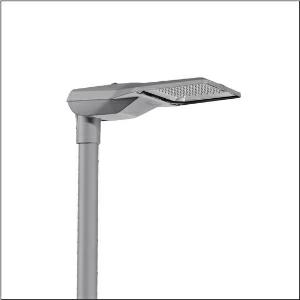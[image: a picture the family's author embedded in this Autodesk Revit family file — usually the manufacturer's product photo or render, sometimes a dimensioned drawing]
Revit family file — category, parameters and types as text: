
# Revit family: streetlight_sl_21_iq_midi___p0_8ab_5xe3r31v08mb_2caf
name_source: partatom
category: Lighting Fixtures
units: mm (PartAtom-declared; Revit-internal decimal feet)

## family parameters
Cut with Voids When Loaded = No
Host = Face
Light Source = No
Part Type = Normal
Room Calculation Point = No
Round Connector Dimension = Use Diameter
Shared = No

## types (1)
- --- (1 x LED, 15920 lm, 129.3 W, 3000K)
    Apparent Load = 129 VA
    CIE Flux Codes = 36 71 98 100 100
    Color Rendering = 70
    Color Temperature = 3000K
    Default Elevation = 1800 mm
    Description = Streetlight SL 21 iQ midi, mast luminaire, primary light control with lens, of PMMA, primary optical cover: cover, of toughened safety glass, transparent, light distribution: P0.8aB, light emission: direct distribution, primary light characteristic: asymmetric, installation type: post-top, side-entry, LED, High Power LED, rated luminous flux: 15.920lm, luminous efficacy: 123lm/W, light colour: 730, colour temperature: 3000K, control gear: iQ-Street Remote, D4i with power reduction, control: pre-setting: logarithmic dimming characteristic, Street-Remote, Auto-Match, Temp-Guard, Lumen-Switch, Night-Set, Smart-Wire, Light-Fading, Desk-Remote (wireless, voltage-free reading and setting of iQ features in the workshop via application-optimized NFC function/RFID function), optimised constant luminous flux control (CLO 2.0), mains connection: 230..240V, AC, 50/60Hz, start of lifetime: 129W, end of service life: 142W, reduction: 56W, luminaire housing, of diecast aluminium, powder-coated, SITECO metallic grey (DB 702S), corrosivity category C5 high according to DIN EN ISO 12944, please order mast flange separately, inclination adjustable: 0°, 5°, 10°, 15°, sealing non-destructively replaceable, multi-level sealing system, length: 644mm, width: 335mm, height: 110mm, mast flange for spigot size: 42mm (side-entry): 5XC10008XM4, 60/48mm (side-entry/post-top): 5XC10108XM2, 76/60mm (side-entry/post-top): 5XC10108XM1, mounting height: 4..8m, Smart Interface above, protection rating (complete): IP66, insulation class (complete): insulation class II (safety insulation), certification: CE, ENEC, ENEC+, VDE, impact resistance: IK10, permissible operating ambient temperature for outdoor applications: -40..+50°C, standard-compliant lighting for roads and squares, packaging unit: 1 piece

Light Distribution: P0.8aB
    Height = 111 mm
    Lamp = 1 x LED
    Lamp Light Flux = 15920 lm
    Lamp Power = 129.3 W
    Lamp count = 1
    Length = 644 mm
    Luminous efficacy = 123 lm/W
    Manufacturer = Siteco
    ModVariant = No
    Model = 5XE3R31V08MB
    Mounting Place = Pole
    Mounting Type = Pole top
    Number of Poles = 1
    OnlyDefault = Yes
    Power Factor = 1
    Product Name = Streetlight SL 21 iQ midi | P0.8aB
    Product group = mast luminaire | pylon top
    ProductGroupID = 6100
    Protection Class = Protection class II
    Protection Degree = IP 66
    RLX_Detail_Level = 1
    RLX_Emergency_Light_Flux = 0 lm
    RLX_Emergency_Type = 0
    RLX_Emergency_Type_DB = No
    RlxData = <blob elided: 90689 chars, md5=8d260d01>
    Socket = socket
    Standby Power = 0 W
    System Light Flux = 15919 lm
    System Power = 129 W
    Type Comments = factory setting: luminous flux: 100 % | dim-lin: 254 | 672 mA
    Type Image = l_1004302.jpg
    URL = http://relux.com
    VarID = @adj_084537
    Voltage = 0 V
    Weight = 0.00 kg
    Width = 336 mm

## geometry (parser evidence)
native form markers: Blend x4, Sweep x10
no freeform markers — native parametric forms only
